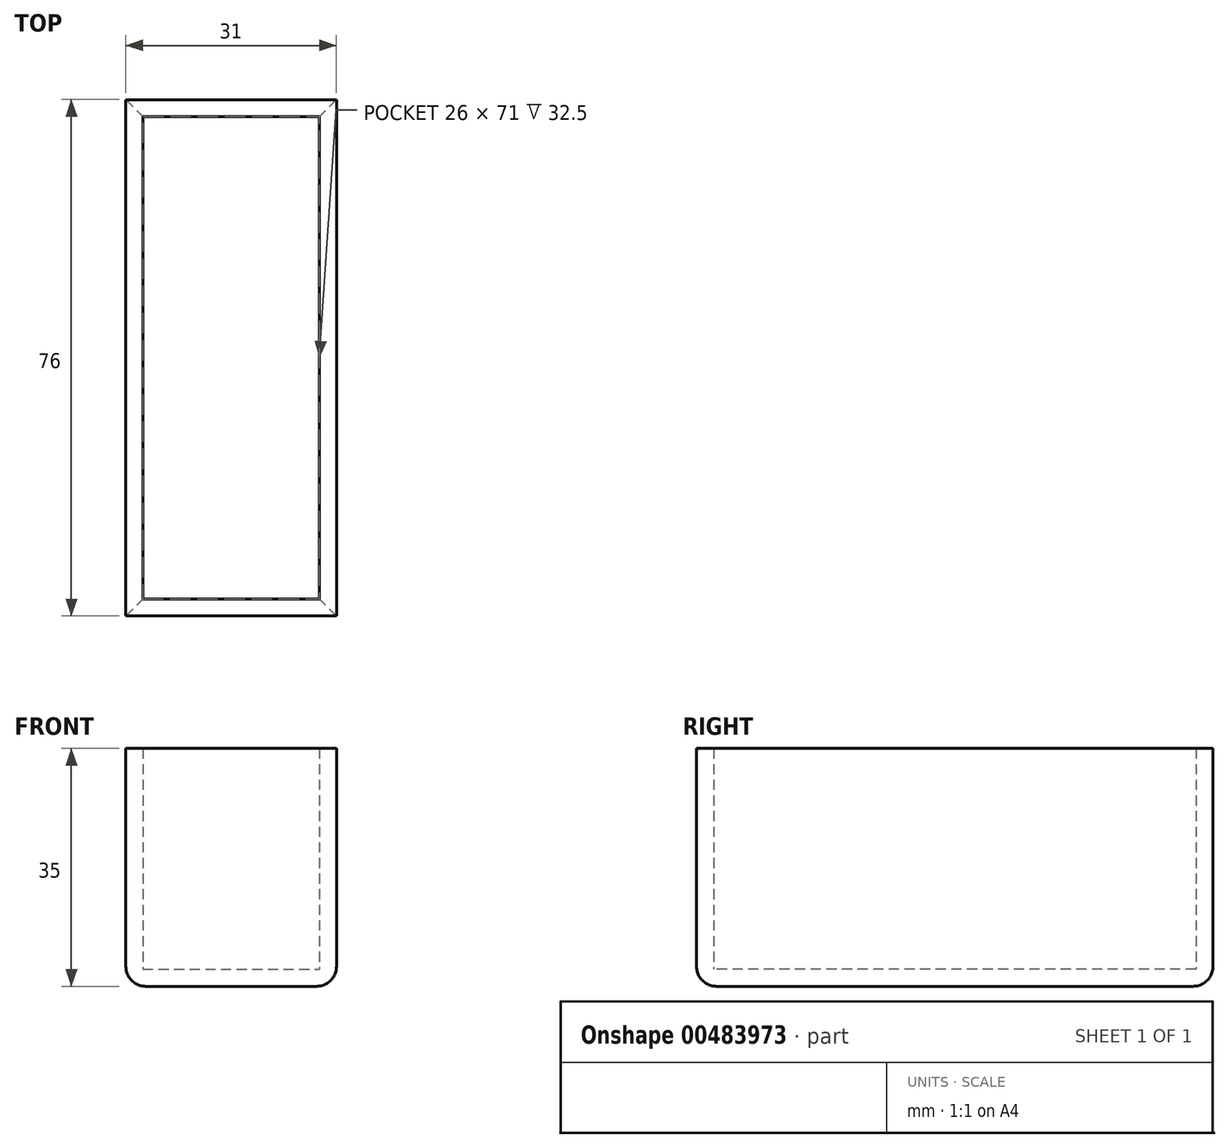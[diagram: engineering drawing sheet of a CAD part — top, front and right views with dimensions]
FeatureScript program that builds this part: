
annotation { "Feature Type Name" : "Feature", "Feature Type Description" : "" }
export const myFeature = defineFeature(function(context is Context, id is Id, definition is map)
    precondition{}
    {
        {
            var Q0;
            Q0=qCreatedBy(makeId("Top.planeOp"),FACE);
            var sketch = newSketch(context, id + "F0", { "sketchPlane" : qUnion([Q0])});
            skLineSegment(sketch, "E0.bottom", {"start": v(-21.13, 32.96) * mm, "end": v(9.87, 32.96) * mm});
            skLineSegment(sketch, "E0.top", {"start": v(-21.13, -43.04) * mm, "end": v(9.87, -43.04) * mm});
            skLineSegment(sketch, "E0.left", {"start": v(-21.13, 32.96) * mm, "end": v(-21.13, -43.04) * mm});
            skLineSegment(sketch, "E0.right", {"start": v(9.87, 32.96) * mm, "end": v(9.87, -43.04) * mm});
            skSolve(sketch);
        }
        {
            var Q0;
            Q0=makeQuery(id+"F0.imprint","IMPRINT",FACE,{"disambiguationData":[TD([[makeQuery(id+"F0.imprint","IMPRINT",EDGE,{"derivedFrom":sQuery(id+"F0.wireOp",EDGE,"E0.bottom")}),-1.0]])]});
            extrude(context, id + "F1", {"entities" : qUnion([Q0]), "depth" : 35 * mm, "offsetDistance" : 25 * mm});
        }
        {
            var Q0;
            Q0=makeQuery(id+"F1.opExtrude","CAP_FACE",FACE,{"disambiguationData":[OSD([sQuery(id+"F0.wireOp",EDGE,"E0.bottom"),sQuery(id+"F0.wireOp",EDGE,"E0.top"),sQuery(id+"F0.wireOp",EDGE,"E0.left"),sQuery(id+"F0.wireOp",EDGE,"E0.right")])],"isStart":false});
            var Q1;
            Q1=makeQuery(id+"F1.opExtrude","SWEPT_BODY",BODY,{"disambiguationData":[OSD([sQuery(id+"F0.wireOp",EDGE,"E0.bottom"),sQuery(id+"F0.wireOp",EDGE,"E0.top"),sQuery(id+"F0.wireOp",EDGE,"E0.left"),sQuery(id+"F0.wireOp",EDGE,"E0.right")])]});
            shell(context, id + "F2", {"entities" : qUnion([Q0]), "parts" : qUnion([Q1]), "thickness" : 2.5 * mm});
        }
        {
            var Q0;
            Q0=makeQuery(id+"F1.opExtrude","CAP_EDGE",EDGE,{"disambiguationData":[OSD([sQuery(id+"F0.wireOp",EDGE,"E0.top")])],"isStart":true});
            var Q1;
            Q1=makeQuery(id+"F1.opExtrude","CAP_EDGE",EDGE,{"disambiguationData":[OSD([sQuery(id+"F0.wireOp",EDGE,"E0.right")])],"isStart":true});
            var Q2;
            Q2=makeQuery(id+"F1.opExtrude","CAP_EDGE",EDGE,{"disambiguationData":[OSD([sQuery(id+"F0.wireOp",EDGE,"E0.left")])],"isStart":true});
            var Q3;
            Q3=makeQuery(id+"F1.opExtrude","CAP_EDGE",EDGE,{"disambiguationData":[OSD([sQuery(id+"F0.wireOp",EDGE,"E0.bottom")])],"isStart":true});
            fillet(context, id + "F3", {"entities" : qUnion([Q0, Q1, Q2, Q3]), "radius" : 2.9 * mm, "tangentPropagation" : true, "allowEdgeOverflow" : false});
        }
    });
